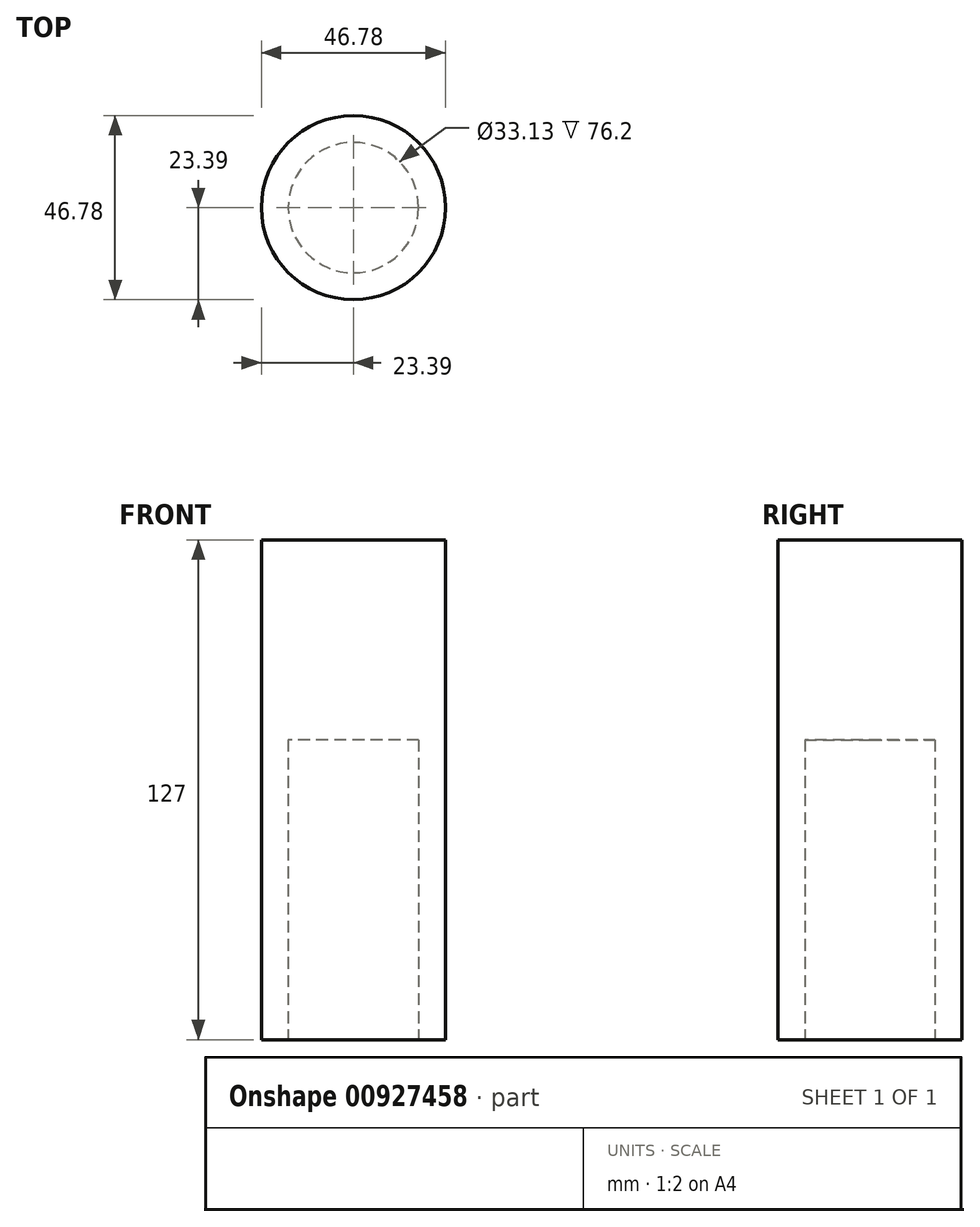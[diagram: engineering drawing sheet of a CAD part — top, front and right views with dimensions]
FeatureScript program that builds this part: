
annotation { "Feature Type Name" : "Feature", "Feature Type Description" : "" }
export const myFeature = defineFeature(function(context is Context, id is Id, definition is map)
    precondition{}
    {
        {
            var Q0;
            Q0=qCreatedBy(makeId("Top.planeOp"),FACE);
            var sketch = newSketch(context, id + "F0", { "sketchPlane" : qUnion([Q0])});
            skCircle(sketch, "E0", {"center": v(0, 0) * mm, "radius": 23.39 * mm});
            skSolve(sketch);
        }
        {
            var Q0;
            Q0 = qSketchRegion(id + "F0", true);
            extrude(context, id + "F1", {"entities" : qUnion([Q0]), "depth" : 127 * mm, "offsetDistance" : 25.4 * mm});
        }
        {
            var Q0;
            Q0=qCreatedBy(makeId("Top.planeOp"),FACE);
            var sketch = newSketch(context, id + "F2", { "sketchPlane" : qUnion([Q0])});
            skCircle(sketch, "E1", {"center": v(0, 0) * mm, "radius": 16.57 * mm});
            skSolve(sketch);
        }
        {
            var Q0;
            Q0 = qSketchRegion(id + "F2", true);
            extrude(context, id + "F3", {"entities" : qUnion([Q0]), "depth" : 76.2 * mm, "offsetDistance" : 25.4 * mm});
        }
        {
            var Q0;
            Q0=makeQuery(id+"F3.opExtrude","SWEPT_BODY",BODY,{"disambiguationData":[OSD([sQuery(id+"F2.wireOp",EDGE,"E1")])]});
            var Q1;
            Q1=makeQuery(id+"F1.opExtrude","SWEPT_BODY",BODY,{"disambiguationData":[OSD([sQuery(id+"F0.wireOp",EDGE,"E0")])]});
            booleanBodies(context, id + "F4", {"operationType" : BooleanOperationType.SUBTRACTION, "tools" : qUnion([Q0]), "targets" : qUnion([Q1]), "offsetAll" : true});
        }
    });
